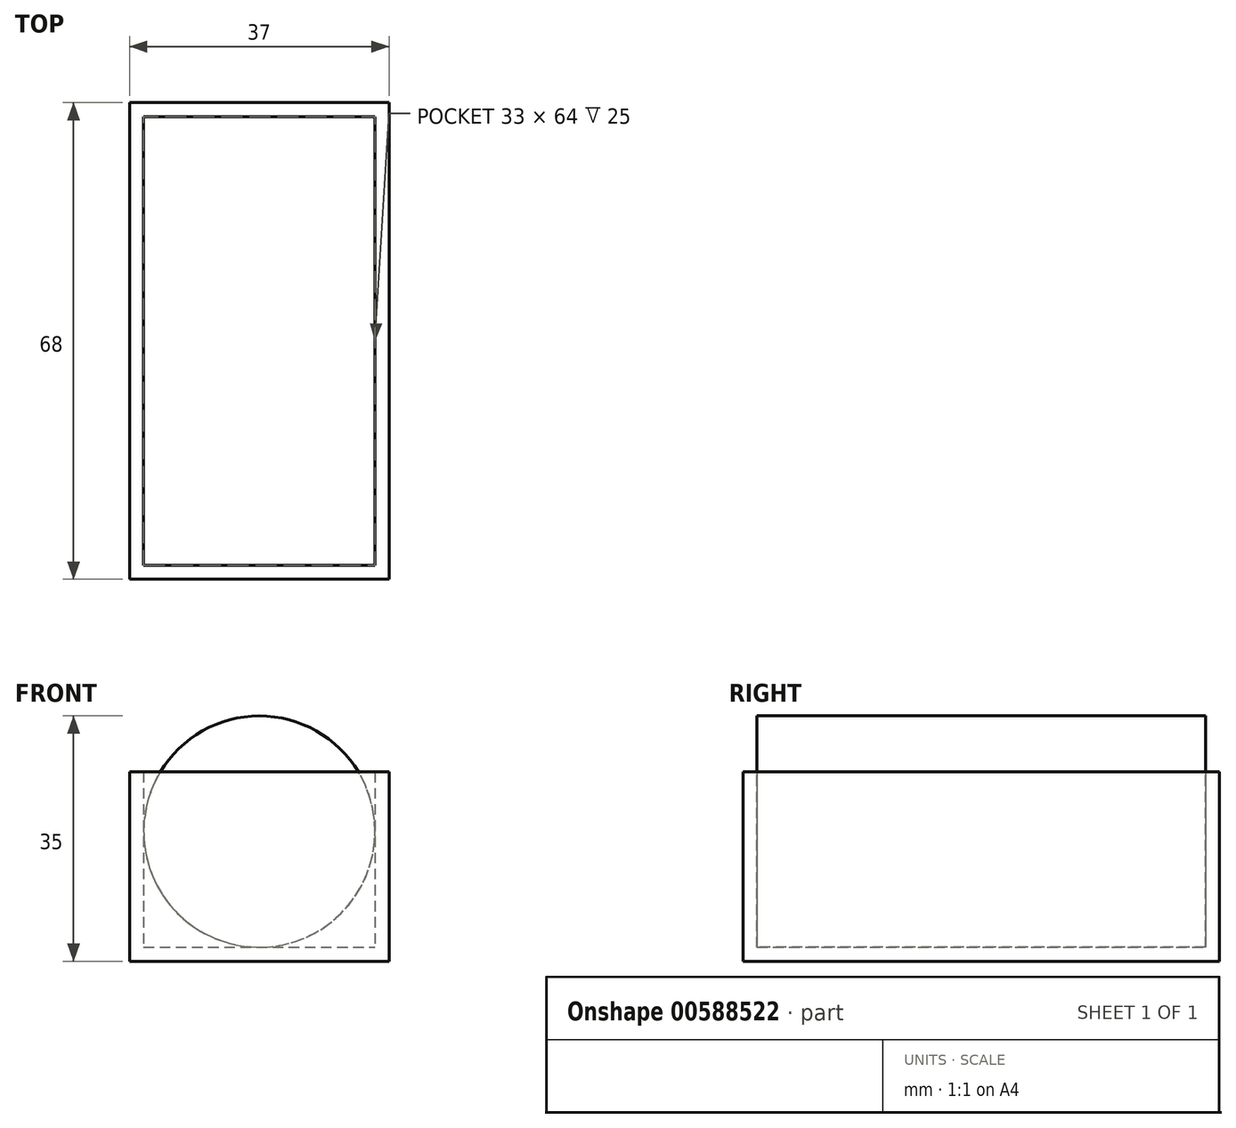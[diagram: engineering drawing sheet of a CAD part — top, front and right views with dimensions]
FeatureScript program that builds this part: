
annotation { "Feature Type Name" : "Feature", "Feature Type Description" : "" }
export const myFeature = defineFeature(function(context is Context, id is Id, definition is map)
    precondition{}
    {
        {
            var Q0;
            Q0=qCreatedBy(makeId("Front.planeOp"),FACE);
            var sketch = newSketch(context, id + "F0", { "sketchPlane" : qUnion([Q0])});
            skCircle(sketch, "E0", {"center": v(0, 18.5) * mm, "radius": 16.5 * mm});
            skSolve(sketch);
        }
        {
            var Q0;
            Q0 = qSketchRegion(id + "F0", true);
            extrude(context, id + "F1", {"entities" : qUnion([Q0]), "endBound" : BoundingType.SYMMETRIC, "oppositeDirection" : true, "depth" : 64 * mm, "offsetDistance" : 25 * mm});
        }
        {
            var Q0;
            Q0=qCreatedBy(makeId("Front.planeOp"),FACE);
            var sketch = newSketch(context, id + "F2", { "sketchPlane" : qUnion([Q0])});
            skLineSegment(sketch, "E1.bottom", {"start": v(-18.5, 27) * mm, "end": v(18.5, 27) * mm});
            skLineSegment(sketch, "E1.top", {"start": v(-18.5, 0) * mm, "end": v(18.5, 0) * mm});
            skLineSegment(sketch, "E1.left", {"start": v(18.5, 27) * mm, "end": v(18.5, 0) * mm});
            skLineSegment(sketch, "E1.right", {"start": v(-18.5, 27) * mm, "end": v(-18.5, 0) * mm});
            skSolve(sketch);
        }
        {
            var Q0;
            Q0=makeQuery(id+"F2.imprint","IMPRINT",FACE,{"disambiguationData":[TD([[makeQuery(id+"F2.imprint","IMPRINT",EDGE,{"derivedFrom":sQuery(id+"F2.wireOp",EDGE,"E1.bottom")}),-1.0]])]});
            extrude(context, id + "F3", {"entities" : qUnion([Q0]), "endBound" : BoundingType.SYMMETRIC, "depth" : 68 * mm, "offsetDistance" : 25 * mm});
        }
        {
            var Q0;
            Q0=makeQuery(id+"F3.opExtrude","SWEPT_FACE",FACE,{"disambiguationData":[OSD([sQuery(id+"F2.wireOp",EDGE,"E1.bottom")])]});
            shell(context, id + "F4", {"entities" : qUnion([Q0]), "thickness" : 2 * mm});
        }
    });
